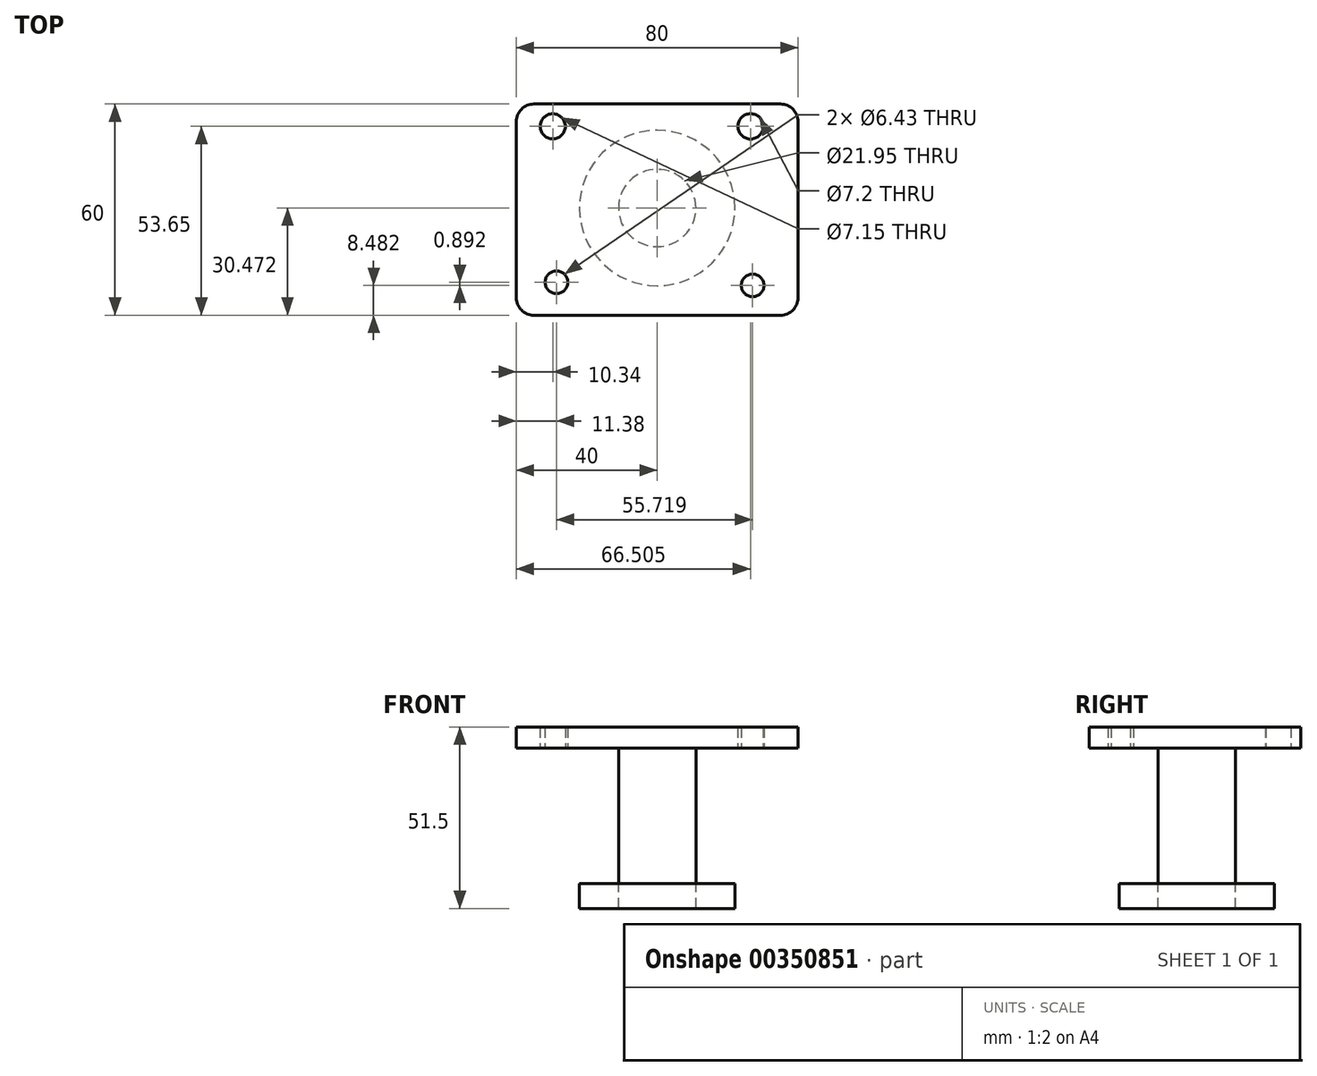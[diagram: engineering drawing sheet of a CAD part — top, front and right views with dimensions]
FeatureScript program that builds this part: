
annotation { "Feature Type Name" : "Feature", "Feature Type Description" : "" }
export const myFeature = defineFeature(function(context is Context, id is Id, definition is map)
    precondition{}
    {
        {
            var Q0;
            Q0=qCreatedBy(makeId("Top.planeOp"),FACE);
            var sketch = newSketch(context, id + "F0", { "sketchPlane" : qUnion([Q0])});
            skLineSegment(sketch, "E0.bottom", {"start": v(-80, -53.65) * mm, "end": v(0, -53.65) * mm});
            skLineSegment(sketch, "E0.top", {"start": v(-80, 6.35) * mm, "end": v(0, 6.35) * mm});
            skLineSegment(sketch, "E0.left", {"start": v(-80, -53.65) * mm, "end": v(-80, 6.35) * mm});
            skLineSegment(sketch, "E0.right", {"start": v(0, -53.65) * mm, "end": v(0, 6.35) * mm});
            skSolve(sketch);
        }
        {
            var Q0;
            Q0=makeQuery(id+"F0.imprint","IMPRINT",FACE,{"disambiguationData":[TD([[makeQuery(id+"F0.imprint","IMPRINT",EDGE,{"derivedFrom":sQuery(id+"F0.wireOp",EDGE,"E0.bottom")}),1.0]])]});
            extrude(context, id + "F1", {"entities" : qUnion([Q0]), "depth" : 6 * mm});
        }
        {
            var Q0;
            Q0=makeQuery(id+"F1.opExtrude","SWEPT_EDGE",EDGE,{"disambiguationData":[OSD([sQuery(id+"F0.wireOp",EDGE,"E0.bottom"),sQuery(id+"F0.wireOp",EDGE,"E0.left")])]});
            fillet(context, id + "F2", {"entities" : qUnion([Q0]), "radius" : 5 * mm, "tangentPropagation" : true, "allowEdgeOverflow" : false});
        }
        {
            var Q0;
            Q0=makeQuery(id+"F1.opExtrude","SWEPT_EDGE",EDGE,{"disambiguationData":[OSD([sQuery(id+"F0.wireOp",EDGE,"E0.top"),sQuery(id+"F0.wireOp",EDGE,"E0.left")])]});
            var Q1;
            Q1=makeQuery(id+"F1.opExtrude","SWEPT_EDGE",EDGE,{"disambiguationData":[OSD([sQuery(id+"F0.wireOp",EDGE,"E0.top"),sQuery(id+"F0.wireOp",EDGE,"E0.right")])]});
            var Q2;
            Q2=makeQuery(id+"F1.opExtrude","SWEPT_EDGE",EDGE,{"disambiguationData":[OSD([sQuery(id+"F0.wireOp",EDGE,"E0.bottom"),sQuery(id+"F0.wireOp",EDGE,"E0.right")])]});
            fillet(context, id + "F3", {"entities" : qUnion([Q0, Q1, Q2]), "radius" : 5 * mm, "tangentPropagation" : true, "allowEdgeOverflow" : false});
        }
        {
            var Q0;
            Q0=makeQuery(id+"F1.opExtrude","CAP_FACE",FACE,{"disambiguationData":[OSD([sQuery(id+"F0.wireOp",EDGE,"E0.bottom"),sQuery(id+"F0.wireOp",EDGE,"E0.top"),sQuery(id+"F0.wireOp",EDGE,"E0.left"),sQuery(id+"F0.wireOp",EDGE,"E0.right")])],"isStart":true});
            var sketch = newSketch(context, id + "F4", { "sketchPlane" : qUnion([Q0])});
            skCircle(sketch, "E1", {"center": v(-40, 23.18) * mm, "radius": 10.97 * mm});
            skPoint(sketch, "E1.centerSnap0", {"position": v(-40, -6.35) * mm});
            skSolve(sketch);
        }
        {
            var Q0;
            Q0=makeQuery(id+"F4.imprint","IMPRINT",FACE,{"disambiguationData":[TD([[makeQuery(id+"F4.imprint","IMPRINT",EDGE,{"derivedFrom":sQuery(id+"F4.wireOp",EDGE,"E1")}),1.0]])]});
            extrude(context, id + "F5", {"entities" : qUnion([Q0]), "operationType" : NewBodyOperationType.ADD, "depth" : 38.5 * mm});
        }
        {
            var Q0;
            Q0=makeQuery(id+"F5.opExtrude","CAP_FACE",FACE,{"disambiguationData":[OSD([sQuery(id+"F4.wireOp",EDGE,"E1")])],"isStart":false});
            var sketch = newSketch(context, id + "F6", { "sketchPlane" : qUnion([Q0])});
            skCircle(sketch, "E2", {"center": v(-40, 23.18) * mm, "radius": 22.07 * mm});
            skSolve(sketch);
        }
        {
            var Q0;
            Q0=makeQuery(id+"F6.imprint","IMPRINT",FACE,{"disambiguationData":[TD([[makeQuery(id+"F6.imprint","IMPRINT",EDGE,{"derivedFrom":sQuery(id+"F6.wireOp",EDGE,"E2")}),1.0]])]});
            extrude(context, id + "F7", {"entities" : qUnion([Q0]), "depth" : 7 * mm});
        }
        {
            var Q0;
            Q0=makeQuery(id+"F1.opExtrude","CAP_FACE",FACE,{"disambiguationData":[OSD([sQuery(id+"F0.wireOp",EDGE,"E0.bottom"),sQuery(id+"F0.wireOp",EDGE,"E0.top"),sQuery(id+"F0.wireOp",EDGE,"E0.left"),sQuery(id+"F0.wireOp",EDGE,"E0.right")])],"isStart":true});
            var sketch = newSketch(context, id + "F8", { "sketchPlane" : qUnion([Q0])});
            skCircle(sketch, "E3", {"center": v(-14.39, 4.75) * mm, "radius": 3.21 * mm});
            skCircle(sketch, "E4", {"center": v(-12.9, 45.17) * mm, "radius": 3.21 * mm});
            skCircle(sketch, "E5", {"center": v(-70.1, 3.86) * mm, "radius": 3.21 * mm});
            skCircle(sketch, "E6", {"center": v(-68.62, 44.28) * mm, "radius": 3.21 * mm});
            skSolve(sketch);
        }
        {
            var Q0;
            Q0=makeQuery(id+"F8.imprint","IMPRINT",FACE,{"disambiguationData":[TD([[makeQuery(id+"F8.imprint","IMPRINT",EDGE,{"derivedFrom":sQuery(id+"F8.wireOp",EDGE,"E6")}),1.0]])]});
            var Q1;
            Q1=makeQuery(id+"F8.imprint","IMPRINT",FACE,{"disambiguationData":[TD([[makeQuery(id+"F8.imprint","IMPRINT",EDGE,{"derivedFrom":sQuery(id+"F8.wireOp",EDGE,"E4")}),1.0]])]});
            var Q2;
            Q2=sQuery(id+"F8.wireOp",EDGE,"E3");
            var Q3;
            Q3=sQuery(id+"F8.wireOp",EDGE,"E4");
            var Q4;
            Q4=sQuery(id+"F8.wireOp",EDGE,"E5");
            var Q5;
            Q5=sQuery(id+"F8.wireOp",EDGE,"E6");
            extrude(context, id + "F9", {"entities" : qUnion([Q0, Q1]), "operationType" : NewBodyOperationType.REMOVE, "surfaceEntities" : qUnion([Q2, Q3, Q4, Q5]), "endBound" : BoundingType.UP_TO_NEXT, "oppositeDirection" : true, "depth" : 25 * mm});
        }
        {
            var Q0;
            Q0=makeQuery(id+"F1.opExtrude","CAP_FACE",FACE,{"disambiguationData":[OSD([sQuery(id+"F0.wireOp",EDGE,"E0.bottom"),sQuery(id+"F0.wireOp",EDGE,"E0.top"),sQuery(id+"F0.wireOp",EDGE,"E0.left"),sQuery(id+"F0.wireOp",EDGE,"E0.right")])],"isStart":true});
            var sketch = newSketch(context, id + "F10", { "sketchPlane" : qUnion([Q0])});
            skCircle(sketch, "E7", {"center": v(-70.25, 0) * mm, "radius": 3.6 * mm});
            skCircle(sketch, "E8", {"center": v(-13.5, 0) * mm, "radius": 3.6 * mm});
            skSolve(sketch);
        }
        {
            var Q0;
            Q0=makeQuery(id+"F10.imprint","IMPRINT",FACE,{"disambiguationData":[TD([[makeQuery(id+"F10.imprint","IMPRINT",EDGE,{"derivedFrom":sQuery(id+"F10.wireOp",EDGE,"E8")}),1.0]])]});
            var Q1;
            Q1=sQuery(id+"F10.wireOp",EDGE,"E8");
            var Q2;
            Q2=sQuery(id+"F10.wireOp",EDGE,"E7");
            extrude(context, id + "F11", {"entities" : qUnion([Q0]), "operationType" : NewBodyOperationType.REMOVE, "surfaceEntities" : qUnion([Q1, Q2]), "endBound" : BoundingType.THROUGH_ALL, "oppositeDirection" : true, "depth" : 25 * mm});
        }
        {
            var Q0;
            Q0=makeQuery(id+"F1.opExtrude","CAP_FACE",FACE,{"disambiguationData":[OSD([sQuery(id+"F0.wireOp",EDGE,"E0.bottom"),sQuery(id+"F0.wireOp",EDGE,"E0.top"),sQuery(id+"F0.wireOp",EDGE,"E0.left"),sQuery(id+"F0.wireOp",EDGE,"E0.right")])],"isStart":true});
            var sketch = newSketch(context, id + "F12", { "sketchPlane" : qUnion([Q0])});
            skCircle(sketch, "E9", {"center": v(-69.66, 0) * mm, "radius": 3.58 * mm});
            skSolve(sketch);
        }
        {
            var Q0;
            Q0=makeQuery(id+"F12.imprint","IMPRINT",FACE,{"disambiguationData":[TD([[makeQuery(id+"F12.imprint","IMPRINT",EDGE,{"derivedFrom":sQuery(id+"F12.wireOp",EDGE,"E9")}),1.0]])]});
            extrude(context, id + "F13", {"entities" : qUnion([Q0]), "operationType" : NewBodyOperationType.REMOVE, "endBound" : BoundingType.THROUGH_ALL, "oppositeDirection" : true, "depth" : 25 * mm});
        }
    });
